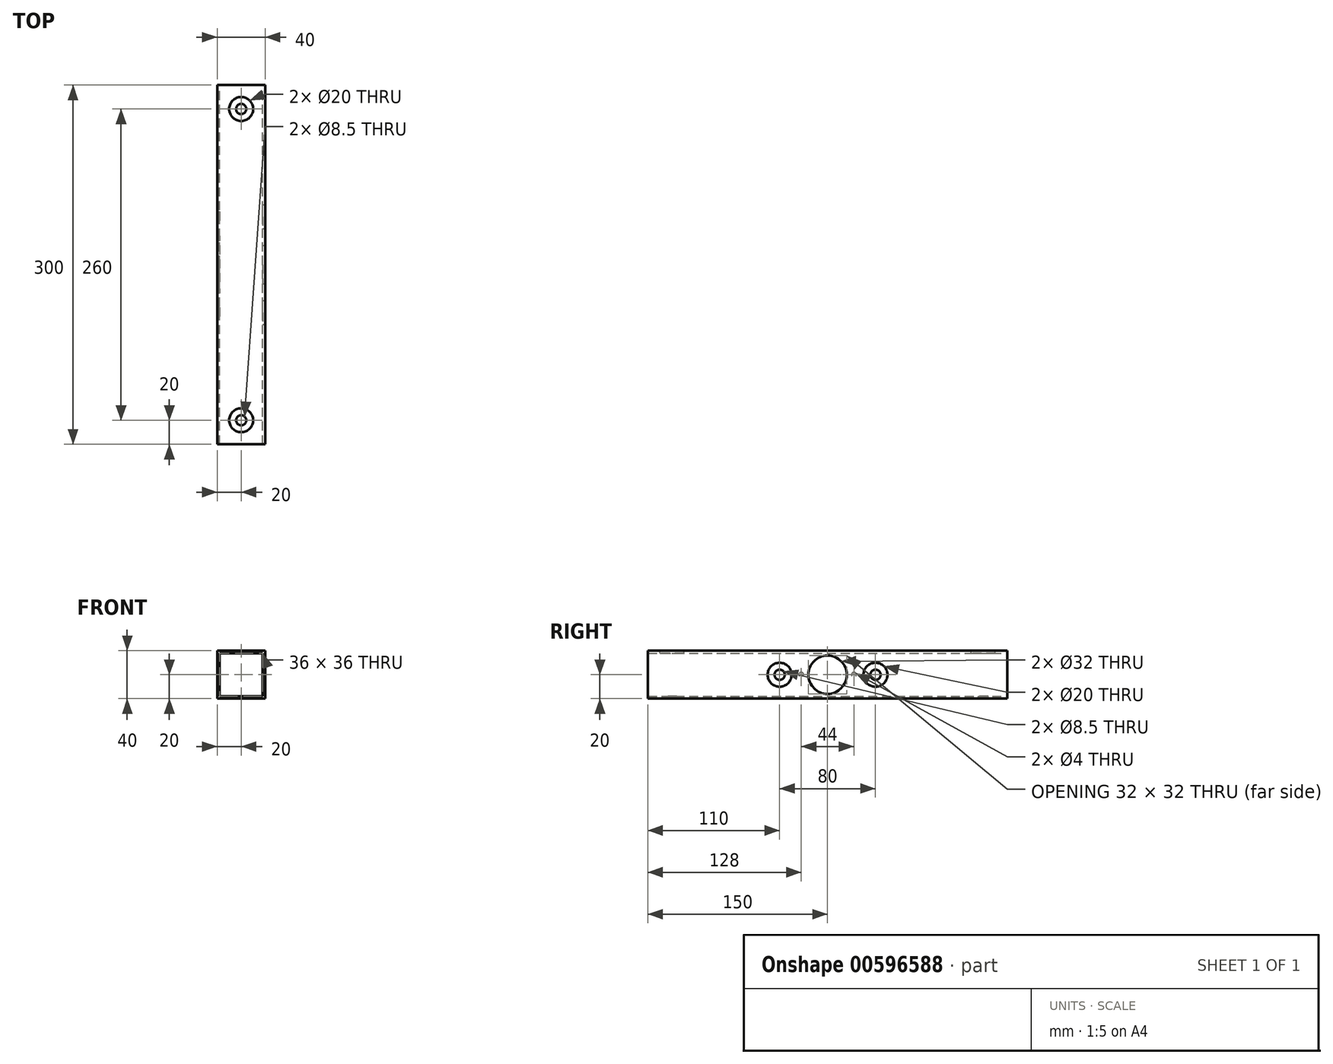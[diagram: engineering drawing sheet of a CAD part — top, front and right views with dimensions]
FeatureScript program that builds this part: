
annotation { "Feature Type Name" : "Feature", "Feature Type Description" : "" }
export const myFeature = defineFeature(function(context is Context, id is Id, definition is map)
    precondition{}
    {
        {
            var Q0;
            Q0=qCreatedBy(makeId("Front.planeOp"),FACE);
            var sketch = newSketch(context, id + "F0", { "sketchPlane" : qUnion([Q0])});
            skLineSegment(sketch, "E0.bottom", {"start": v(0, 0) * mm, "end": v(40, 0) * mm});
            skLineSegment(sketch, "E0.top", {"start": v(0, 40) * mm, "end": v(40, 40) * mm});
            skLineSegment(sketch, "E0.left", {"start": v(0, 0) * mm, "end": v(0, 40) * mm});
            skLineSegment(sketch, "E0.right", {"start": v(40, 0) * mm, "end": v(40, 40) * mm});
            skLineSegment(sketch, "E1.0", {"start": v(2, 38) * mm, "end": v(38, 38) * mm});
            skLineSegment(sketch, "E2.0", {"start": v(2, 2) * mm, "end": v(2, 38) * mm});
            skLineSegment(sketch, "E3.0", {"start": v(38, 2) * mm, "end": v(38, 38) * mm});
            skLineSegment(sketch, "E4.0", {"start": v(2, 2) * mm, "end": v(38, 2) * mm});
            skSolve(sketch);
        }
        {
            var Q0;
            Q0 = qSketchRegion(id + "F0", true);
            extrude(context, id + "F1", {"entities" : qUnion([Q0]), "depth" : 300 * mm, "offsetDistance" : 25 * mm});
        }
        {
            var Q0;
            Q0=makeQuery(id+"F1.opExtrude","SWEPT_FACE",FACE,{"disambiguationData":[OSD([sQuery(id+"F0.wireOp",EDGE,"E0.right")])]});
            var sketch = newSketch(context, id + "F2", { "sketchPlane" : qUnion([Q0])});
            skCircle(sketch, "E5", {"center": v(-150, 20) * mm, "radius": 16 * mm});
            skPoint(sketch, "E5.centerSnap0", {"position": v(0, 20) * mm});
            skPoint(sketch, "E5.centerSnap1", {"position": v(-150, 40) * mm});
            skCircle(sketch, "E6", {"center": v(-190, 20) * mm, "radius": 10 * mm});
            skCircle(sketch, "E7", {"center": v(-110, 20) * mm, "radius": 10 * mm});
            skSolve(sketch);
        }
        {
            var Q0;
            Q0 = qSketchRegion(id + "F2", true);
            extrude(context, id + "F3", {"entities" : qUnion([Q0]), "operationType" : NewBodyOperationType.REMOVE, "oppositeDirection" : true, "depth" : 25 * mm, "offsetDistance" : 25 * mm});
        }
        {
            var Q0;
            Q0=makeQuery(id+"F1.opExtrude","SWEPT_FACE",FACE,{"disambiguationData":[OSD([sQuery(id+"F0.wireOp",EDGE,"E2.0")])]});
            var sketch = newSketch(context, id + "F4", { "sketchPlane" : qUnion([Q0])});
            skCircle(sketch, "E8", {"center": v(-150, 20) * mm, "radius": 16 * mm});
            skPoint(sketch, "E8.centerSnap0", {"position": v(0, 20) * mm});
            skPoint(sketch, "E8.centerSnap1", {"position": v(-150, 38) * mm});
            skCircle(sketch, "E9", {"center": v(-190, 20) * mm, "radius": 4.25 * mm});
            skCircle(sketch, "E10", {"center": v(-110, 20) * mm, "radius": 4.25 * mm});
            skSolve(sketch);
        }
        {
            var Q0;
            Q0 = qSketchRegion(id + "F4", true);
            extrude(context, id + "F5", {"entities" : qUnion([Q0]), "operationType" : NewBodyOperationType.REMOVE, "oppositeDirection" : true, "depth" : 25 * mm, "offsetDistance" : 25 * mm});
        }
        {
            var Q0;
            Q0=makeQuery(id+"F1.opExtrude","SWEPT_FACE",FACE,{"disambiguationData":[OSD([sQuery(id+"F0.wireOp",EDGE,"E0.top")])]});
            var sketch = newSketch(context, id + "F6", { "sketchPlane" : qUnion([Q0])});
            skCircle(sketch, "E11", {"center": v(20, -280) * mm, "radius": 10 * mm});
            skPoint(sketch, "E11.centerSnap0", {"position": v(20, -300) * mm});
            skCircle(sketch, "E12", {"center": v(20, -20) * mm, "radius": 10 * mm});
            skSolve(sketch);
        }
        {
            var Q0;
            Q0 = qSketchRegion(id + "F6", true);
            extrude(context, id + "F7", {"entities" : qUnion([Q0]), "operationType" : NewBodyOperationType.REMOVE, "oppositeDirection" : true, "depth" : 25 * mm, "offsetDistance" : 25 * mm});
        }
        {
            var Q0;
            Q0=makeQuery(id+"F1.opExtrude","SWEPT_FACE",FACE,{"disambiguationData":[OSD([sQuery(id+"F0.wireOp",EDGE,"E4.0")])]});
            var sketch = newSketch(context, id + "F8", { "sketchPlane" : qUnion([Q0])});
            skCircle(sketch, "E13", {"center": v(20, -280) * mm, "radius": 4.25 * mm});
            skPoint(sketch, "E13.centerSnap0", {"position": v(20, -300) * mm});
            skCircle(sketch, "E14", {"center": v(20, -20) * mm, "radius": 4.25 * mm});
            skPoint(sketch, "E14.centerSnap0", {"position": v(20, 0) * mm});
            skSolve(sketch);
        }
        {
            var Q0;
            Q0 = qSketchRegion(id + "F8", true);
            extrude(context, id + "F9", {"entities" : qUnion([Q0]), "operationType" : NewBodyOperationType.REMOVE, "oppositeDirection" : true, "depth" : 25 * mm, "offsetDistance" : 25 * mm});
        }
        {
            var Q0;
            Q0=makeQuery(id+"F1.opExtrude","SWEPT_FACE",FACE,{"disambiguationData":[OSD([sQuery(id+"F0.wireOp",EDGE,"E0.left")])]});
            var sketch = newSketch(context, id + "F10", { "sketchPlane" : qUnion([Q0])});
            skCircle(sketch, "E15", {"center": v(150, 20) * mm, "radius": 22 * mm, "construction": true});
            skCircle(sketch, "E16", {"center": v(172, 20) * mm, "radius": 2 * mm});
            skCircle(sketch, "E17", {"center": v(128, 20) * mm, "radius": 2 * mm});
            skSolve(sketch);
        }
        {
            var Q0;
            Q0=makeQuery(id+"F10.imprint","IMPRINT",FACE,{"disambiguationData":[TD([[makeQuery(id+"F10.imprint","IMPRINT",EDGE,{"derivedFrom":sQuery(id+"F10.wireOp",EDGE,"E17")}),1.0]])]});
            var Q1;
            Q1=makeQuery(id+"F10.imprint","IMPRINT",FACE,{"disambiguationData":[TD([[makeQuery(id+"F10.imprint","IMPRINT",EDGE,{"derivedFrom":sQuery(id+"F10.wireOp",EDGE,"E16")}),1.0]])]});
            extrude(context, id + "F11", {"entities" : qUnion([Q0, Q1]), "operationType" : NewBodyOperationType.REMOVE, "oppositeDirection" : true, "depth" : 25 * mm, "offsetDistance" : 25 * mm});
        }
    });
